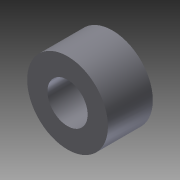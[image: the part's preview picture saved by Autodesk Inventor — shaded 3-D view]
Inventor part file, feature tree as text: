
AUTODESK INVENTOR PART (.ipt)
format: ipt  version: 2014 SP1 (Build 180222100, 222)  size: 80,896 bytes
history: native  units: in
note: dims shown in document units (in); Inventor stores cm internally (conversion verified against a paired STEP export)
features: extrude x1, sketch x1
ambient origin geometry x8: Origin, YZ Plane, XZ Plane, XY Plane, X Axis, Y Axis, Z Axis, Center Point
bodies: Solid1 (feature_tree)
feature tree (2):
  extrude  "Extrusion1"  Depth=0.25in
  sketch  "Sketch1"  dims[d0=0.45in d1=0.224in d2=0.25in d3=0.0in]
